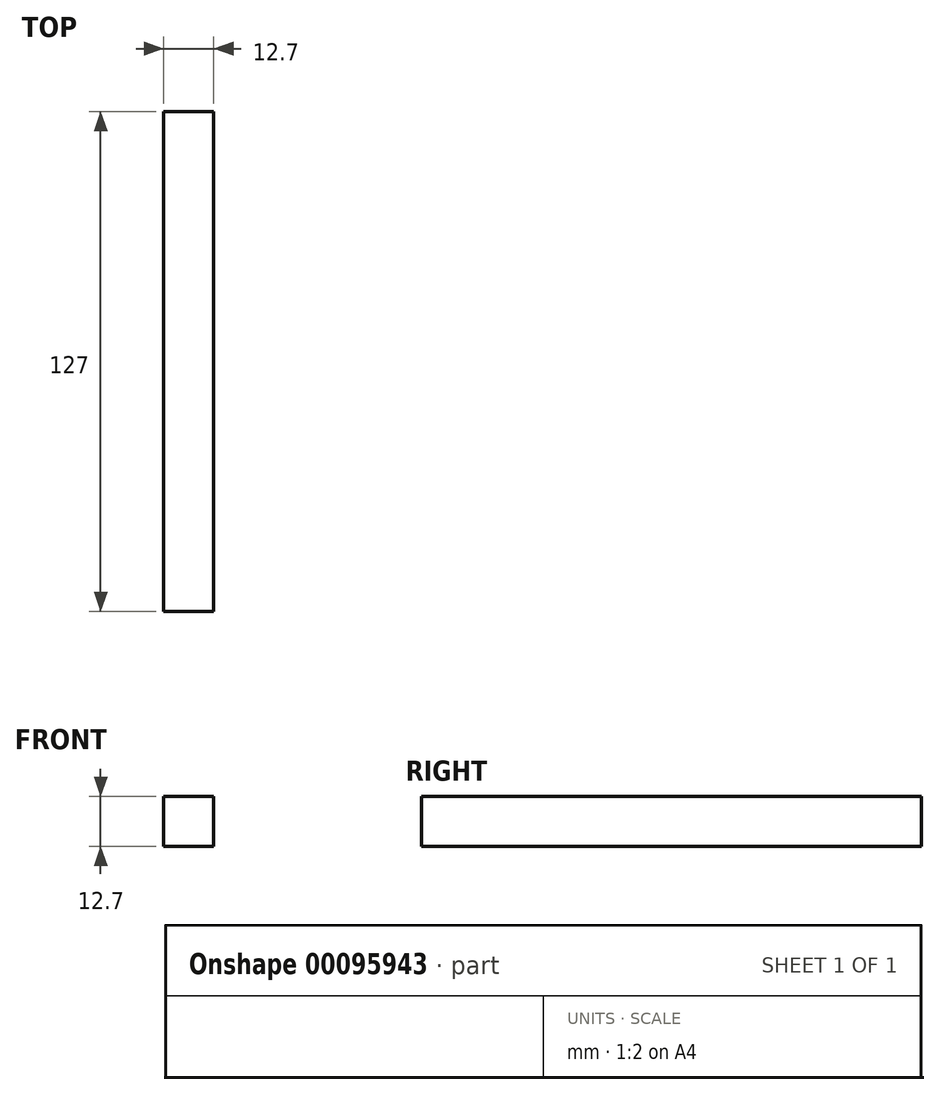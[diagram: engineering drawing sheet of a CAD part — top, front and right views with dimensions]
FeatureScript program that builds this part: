
annotation { "Feature Type Name" : "Feature", "Feature Type Description" : "" }
export const myFeature = defineFeature(function(context is Context, id is Id, definition is map)
    precondition{}
    {
        {
            var Q0;
            Q0=qCreatedBy(makeId("Right.planeOp"),FACE);
            var sketch = newSketch(context, id + "F0", { "sketchPlane" : qUnion([Q0])});
            skLineSegment(sketch, "E0.bottom", {"start": v(-63.5, -71.97) * mm, "end": v(63.5, -71.97) * mm});
            skLineSegment(sketch, "E0.top", {"start": v(-63.5, -84.67) * mm, "end": v(63.5, -84.67) * mm});
            skLineSegment(sketch, "E0.left", {"start": v(-63.5, -71.97) * mm, "end": v(-63.5, -84.67) * mm});
            skLineSegment(sketch, "E0.right", {"start": v(63.5, -71.97) * mm, "end": v(63.5, -84.67) * mm});
            skPoint(sketch, "E0.middle", {"position": v(0, -78.32) * mm});
            skSolve(sketch);
        }
        {
            var Q0;
            Q0=makeQuery(id+"F0.imprint","IMPRINT",FACE,{"disambiguationData":[TD([[makeQuery(id+"F0.imprint","IMPRINT",EDGE,{"derivedFrom":sQuery(id+"F0.wireOp",EDGE,"E0.bottom")}),-1.0]])]});
            extrude(context, id + "F1", {"entities" : qUnion([Q0]), "endBound" : BoundingType.SYMMETRIC, "depth" : 12.7 * mm});
        }
    });
